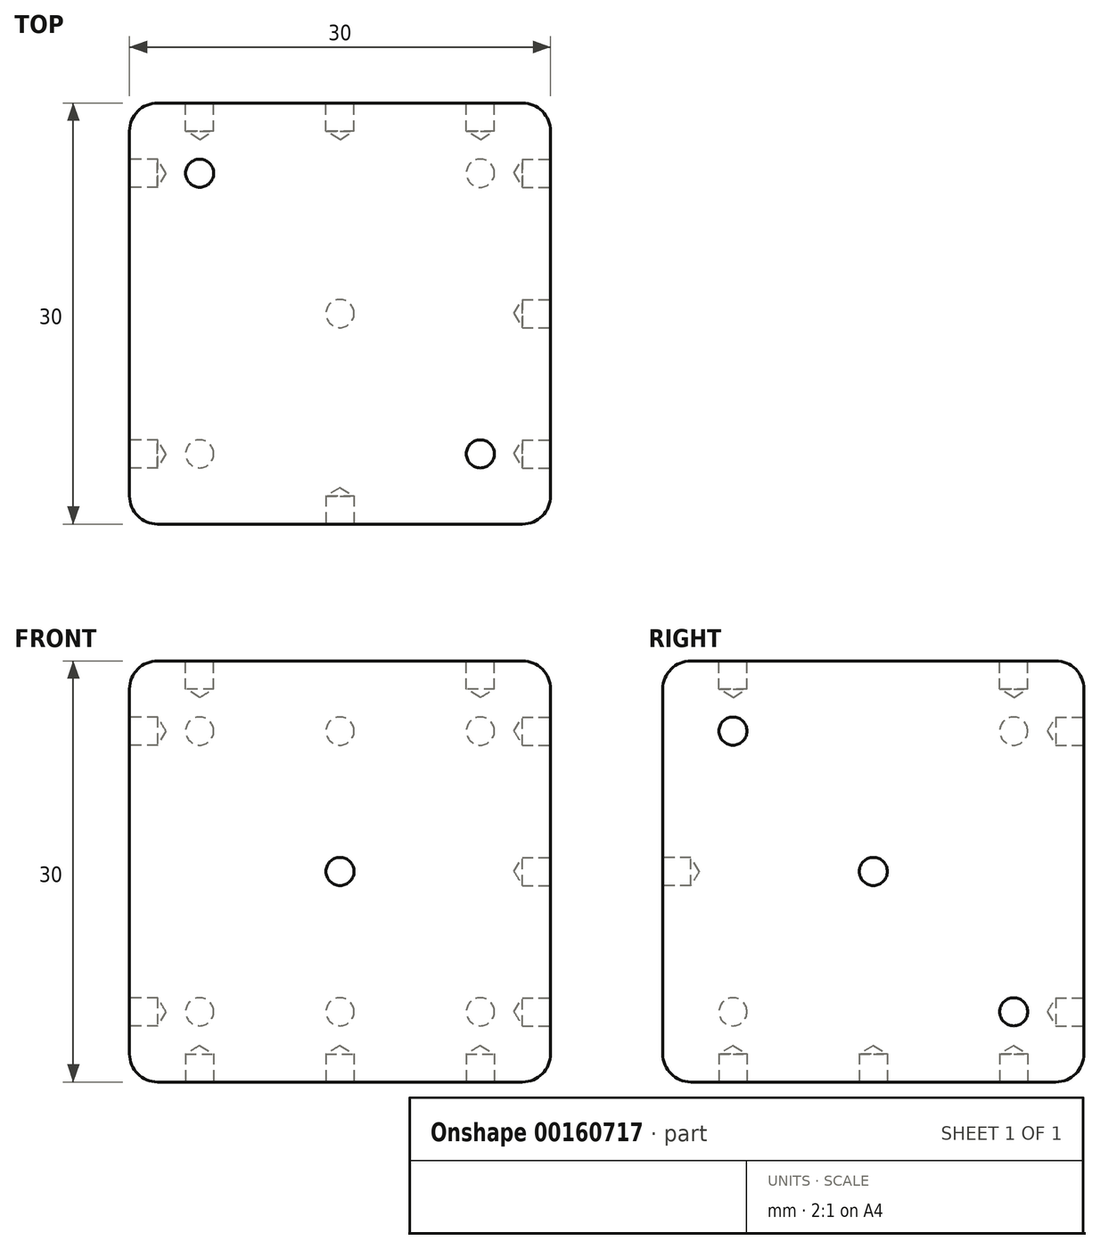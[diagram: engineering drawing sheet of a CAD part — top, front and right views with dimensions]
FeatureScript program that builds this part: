
annotation { "Feature Type Name" : "Feature", "Feature Type Description" : "" }
export const myFeature = defineFeature(function(context is Context, id is Id, definition is map)
    precondition{}
    {
        {
            var Q0;
            Q0=qCreatedBy(makeId("Front.planeOp"),FACE);
            var sketch = newSketch(context, id + "F0", { "sketchPlane" : qUnion([Q0])});
            skLineSegment(sketch, "E0.bottom", {"start": v(15, 15) * mm, "end": v(-15, 15) * mm});
            skLineSegment(sketch, "E0.top", {"start": v(15, -15) * mm, "end": v(-15, -15) * mm});
            skLineSegment(sketch, "E0.left", {"start": v(15, 15) * mm, "end": v(15, -15) * mm});
            skLineSegment(sketch, "E0.right", {"start": v(-15, 15) * mm, "end": v(-15, -15) * mm});
            skPoint(sketch, "E0.middle", {"position": v(0, 0) * mm});
            skSolve(sketch);
        }
        {
            var Q0;
            Q0 = qSketchRegion(id + "F0", true);
            extrude(context, id + "F1", {"entities" : qUnion([Q0]), "endBound" : BoundingType.SYMMETRIC, "depth" : 30 * mm});
        }
        {
            var Q0;
            Q0=makeQuery(id+"F1.opExtrude","CAP_EDGE",EDGE,{"disambiguationData":[OSD([sQuery(id+"F0.wireOp",EDGE,"E0.bottom")])],"isStart":false});
            var Q1;
            Q1=makeQuery(id+"F1.opExtrude","SWEPT_EDGE",EDGE,{"disambiguationData":[OSD([sQuery(id+"F0.wireOp",EDGE,"E0.bottom"),sQuery(id+"F0.wireOp",EDGE,"E0.left")])]});
            var Q2;
            Q2=makeQuery(id+"F1.opExtrude","CAP_EDGE",EDGE,{"disambiguationData":[OSD([sQuery(id+"F0.wireOp",EDGE,"E0.bottom")])],"isStart":true});
            var Q3;
            Q3=makeQuery(id+"F1.opExtrude","SWEPT_EDGE",EDGE,{"disambiguationData":[OSD([sQuery(id+"F0.wireOp",EDGE,"E0.bottom"),sQuery(id+"F0.wireOp",EDGE,"E0.right")])]});
            var Q4;
            Q4=makeQuery(id+"F1.opExtrude","CAP_EDGE",EDGE,{"disambiguationData":[OSD([sQuery(id+"F0.wireOp",EDGE,"E0.left")])],"isStart":false});
            var Q5;
            Q5=makeQuery(id+"F1.opExtrude","CAP_EDGE",EDGE,{"disambiguationData":[OSD([sQuery(id+"F0.wireOp",EDGE,"E0.top")])],"isStart":false});
            var Q6;
            Q6=makeQuery(id+"F1.opExtrude","CAP_EDGE",EDGE,{"disambiguationData":[OSD([sQuery(id+"F0.wireOp",EDGE,"E0.right")])],"isStart":false});
            var Q7;
            Q7=makeQuery(id+"F1.opExtrude","SWEPT_EDGE",EDGE,{"disambiguationData":[OSD([sQuery(id+"F0.wireOp",EDGE,"E0.top"),sQuery(id+"F0.wireOp",EDGE,"E0.left")])]});
            var Q8;
            Q8=makeQuery(id+"F1.opExtrude","CAP_EDGE",EDGE,{"disambiguationData":[OSD([sQuery(id+"F0.wireOp",EDGE,"E0.left")])],"isStart":true});
            var Q9;
            Q9=makeQuery(id+"F1.opExtrude","SWEPT_EDGE",EDGE,{"disambiguationData":[OSD([sQuery(id+"F0.wireOp",EDGE,"E0.top"),sQuery(id+"F0.wireOp",EDGE,"E0.right")])]});
            var Q10;
            Q10=makeQuery(id+"F1.opExtrude","CAP_EDGE",EDGE,{"disambiguationData":[OSD([sQuery(id+"F0.wireOp",EDGE,"E0.top")])],"isStart":true});
            var Q11;
            Q11=makeQuery(id+"F1.opExtrude","CAP_EDGE",EDGE,{"disambiguationData":[OSD([sQuery(id+"F0.wireOp",EDGE,"E0.right")])],"isStart":true});
            fillet(context, id + "F2", {"entities" : qUnion([Q0, Q1, Q2, Q3, Q4, Q5, Q6, Q7, Q8, Q9, Q10, Q11]), "radius" : 2 * mm, "tangentPropagation" : true, "allowEdgeOverflow" : false});
        }
        {
            var Q0;
            Q0=makeQuery(id+"F1.opExtrude","CAP_FACE",FACE,{"disambiguationData":[OSD([sQuery(id+"F0.wireOp",EDGE,"E0.bottom"),sQuery(id+"F0.wireOp",EDGE,"E0.top"),sQuery(id+"F0.wireOp",EDGE,"E0.left"),sQuery(id+"F0.wireOp",EDGE,"E0.right")])],"isStart":false});
            var sketch = newSketch(context, id + "F3", { "sketchPlane" : qUnion([Q0])});
            skCircle(sketch, "E1", {"center": v(0, 0) * mm, "radius": 1 * mm});
            skSolve(sketch);
        }
        {
            var Q0;
            Q0=sQuery(id+"F3.wireOp",VERTEX,"E1.center");
            var Q1;
            Q1=makeQuery(id+"F1.opExtrude","SWEPT_BODY",BODY,{"disambiguationData":[OSD([sQuery(id+"F0.wireOp",EDGE,"E0.bottom"),sQuery(id+"F0.wireOp",EDGE,"E0.top"),sQuery(id+"F0.wireOp",EDGE,"E0.left"),sQuery(id+"F0.wireOp",EDGE,"E0.right")])]});
            hole(context, id + "F4", {"style" : HoleStyle.SIMPLE, "endStyle" : HoleEndStyle.BLIND, "holeDiameter" : 2 * mm, "holeDepth" : 2 * mm, "locations" : qUnion([Q0]), "scope" : qUnion([Q1])});
        }
        {
            var Q0;
            Q0=makeQuery(id+"F1.opExtrude","SWEPT_FACE",FACE,{"disambiguationData":[OSD([sQuery(id+"F0.wireOp",EDGE,"E0.left")])]});
            var sketch = newSketch(context, id + "F5", { "sketchPlane" : qUnion([Q0])});
            skPoint(sketch, "E2", {"position": v(-10, 10) * mm});
            skPoint(sketch, "E3", {"position": v(10, -10) * mm});
            skPoint(sketch, "E4", {"position": v(0, 0) * mm});
            skSolve(sketch);
        }
        {
            var Q0;
            Q0=makeQuery(id+"F1.opExtrude","SWEPT_FACE",FACE,{"disambiguationData":[OSD([sQuery(id+"F0.wireOp",EDGE,"E0.bottom")])]});
            var sketch = newSketch(context, id + "F6", { "sketchPlane" : qUnion([Q0])});
            skPoint(sketch, "E5", {"position": v(-10, 10) * mm});
            skPoint(sketch, "E6", {"position": v(10, -10) * mm});
            skSolve(sketch);
        }
        {
            var Q0;
            Q0=makeQuery(id+"F1.opExtrude","SWEPT_FACE",FACE,{"disambiguationData":[OSD([sQuery(id+"F0.wireOp",EDGE,"E0.right")])]});
            var sketch = newSketch(context, id + "F7", { "sketchPlane" : qUnion([Q0])});
            skPoint(sketch, "E7", {"position": v(-10, 10) * mm});
            skPoint(sketch, "E8", {"position": v(10, 10) * mm});
            skPoint(sketch, "E9", {"position": v(10, -10) * mm});
            skPoint(sketch, "E10", {"position": v(-10, -10) * mm});
            skSolve(sketch);
        }
        {
            var Q0;
            Q0=makeQuery(id+"F1.opExtrude","CAP_FACE",FACE,{"disambiguationData":[OSD([sQuery(id+"F0.wireOp",EDGE,"E0.bottom"),sQuery(id+"F0.wireOp",EDGE,"E0.top"),sQuery(id+"F0.wireOp",EDGE,"E0.left"),sQuery(id+"F0.wireOp",EDGE,"E0.right")])],"isStart":true});
            var sketch = newSketch(context, id + "F8", { "sketchPlane" : qUnion([Q0])});
            skPoint(sketch, "E11", {"position": v(-10, -10) * mm});
            skPoint(sketch, "E12", {"position": v(10, -10) * mm});
            skPoint(sketch, "E13", {"position": v(10, 10) * mm});
            skPoint(sketch, "E14", {"position": v(0, 10) * mm});
            skPoint(sketch, "E15", {"position": v(-10, 10) * mm});
            skPoint(sketch, "E16", {"position": v(0, -10) * mm});
            skSolve(sketch);
        }
        {
            var Q0;
            Q0=makeQuery(id+"F1.opExtrude","SWEPT_FACE",FACE,{"disambiguationData":[OSD([sQuery(id+"F0.wireOp",EDGE,"E0.top")])]});
            var sketch = newSketch(context, id + "F9", { "sketchPlane" : qUnion([Q0])});
            skPoint(sketch, "E17", {"position": v(0, 0) * mm});
            skPoint(sketch, "E18", {"position": v(-10, 10) * mm});
            skPoint(sketch, "E19", {"position": v(10, 10) * mm});
            skPoint(sketch, "E20", {"position": v(10, -10) * mm});
            skPoint(sketch, "E21", {"position": v(-10, -10) * mm});
            skSolve(sketch);
        }
        {
            var Q0;
            Q0=sQuery(id+"F5.wireOp",VERTEX,"E2");
            var Q1;
            Q1=sQuery(id+"F5.wireOp",VERTEX,"E3");
            var Q2;
            Q2=sQuery(id+"F5.wireOp",VERTEX,"E4");
            var Q3;
            Q3=makeQuery(id+"F1.opExtrude","SWEPT_BODY",BODY,{"disambiguationData":[OSD([sQuery(id+"F0.wireOp",EDGE,"E0.bottom"),sQuery(id+"F0.wireOp",EDGE,"E0.top"),sQuery(id+"F0.wireOp",EDGE,"E0.left"),sQuery(id+"F0.wireOp",EDGE,"E0.right")])]});
            hole(context, id + "F10", {"style" : HoleStyle.SIMPLE, "endStyle" : HoleEndStyle.BLIND, "holeDiameter" : 2 * mm, "holeDepth" : 2 * mm, "startFromSketch" : true, "locations" : qUnion([Q0, Q1, Q2]), "scope" : qUnion([Q3])});
        }
        {
            var Q0;
            Q0=sQuery(id+"F8.wireOp",VERTEX,"E15");
            var Q1;
            Q1=sQuery(id+"F8.wireOp",VERTEX,"E14");
            var Q2;
            Q2=sQuery(id+"F8.wireOp",VERTEX,"E13");
            var Q3;
            Q3=sQuery(id+"F8.wireOp",VERTEX,"E12");
            var Q4;
            Q4=sQuery(id+"F8.wireOp",VERTEX,"E16");
            var Q5;
            Q5=sQuery(id+"F8.wireOp",VERTEX,"E11");
            var Q6;
            Q6=makeQuery(id+"F1.opExtrude","SWEPT_BODY",BODY,{"disambiguationData":[OSD([sQuery(id+"F0.wireOp",EDGE,"E0.bottom"),sQuery(id+"F0.wireOp",EDGE,"E0.top"),sQuery(id+"F0.wireOp",EDGE,"E0.left"),sQuery(id+"F0.wireOp",EDGE,"E0.right")])]});
            hole(context, id + "F11", {"style" : HoleStyle.SIMPLE, "endStyle" : HoleEndStyle.BLIND, "holeDiameter" : 2 * mm, "holeDepth" : 2 * mm, "startFromSketch" : true, "locations" : qUnion([Q0, Q1, Q2, Q3, Q4, Q5]), "scope" : qUnion([Q6])});
        }
        {
            var Q0;
            Q0=sQuery(id+"F6.wireOp",VERTEX,"E6");
            var Q1;
            Q1=sQuery(id+"F6.wireOp",VERTEX,"E5");
            var Q2;
            Q2=makeQuery(id+"F1.opExtrude","SWEPT_BODY",BODY,{"disambiguationData":[OSD([sQuery(id+"F0.wireOp",EDGE,"E0.bottom"),sQuery(id+"F0.wireOp",EDGE,"E0.top"),sQuery(id+"F0.wireOp",EDGE,"E0.left"),sQuery(id+"F0.wireOp",EDGE,"E0.right")])]});
            hole(context, id + "F12", {"style" : HoleStyle.SIMPLE, "endStyle" : HoleEndStyle.BLIND, "holeDiameter" : 2 * mm, "holeDepth" : 2 * mm, "startFromSketch" : true, "locations" : qUnion([Q0, Q1]), "scope" : qUnion([Q2])});
        }
        {
            var Q0;
            Q0=sQuery(id+"F7.wireOp",VERTEX,"E8");
            var Q1;
            Q1=sQuery(id+"F7.wireOp",VERTEX,"E7");
            var Q2;
            Q2=sQuery(id+"F7.wireOp",VERTEX,"E9");
            var Q3;
            Q3=sQuery(id+"F7.wireOp",VERTEX,"E10");
            var Q4;
            Q4=makeQuery(id+"F1.opExtrude","SWEPT_BODY",BODY,{"disambiguationData":[OSD([sQuery(id+"F0.wireOp",EDGE,"E0.bottom"),sQuery(id+"F0.wireOp",EDGE,"E0.top"),sQuery(id+"F0.wireOp",EDGE,"E0.left"),sQuery(id+"F0.wireOp",EDGE,"E0.right")])]});
            hole(context, id + "F13", {"style" : HoleStyle.SIMPLE, "endStyle" : HoleEndStyle.BLIND, "holeDiameter" : 2 * mm, "holeDepth" : 2 * mm, "startFromSketch" : true, "locations" : qUnion([Q0, Q1, Q2, Q3]), "scope" : qUnion([Q4])});
        }
        {
            var Q0;
            Q0=sQuery(id+"F9.wireOp",VERTEX,"E18");
            var Q1;
            Q1=sQuery(id+"F9.wireOp",VERTEX,"E21");
            var Q2;
            Q2=sQuery(id+"F9.wireOp",VERTEX,"E17");
            var Q3;
            Q3=sQuery(id+"F9.wireOp",VERTEX,"E20");
            var Q4;
            Q4=sQuery(id+"F9.wireOp",VERTEX,"E19");
            var Q5;
            Q5=makeQuery(id+"F1.opExtrude","SWEPT_BODY",BODY,{"disambiguationData":[OSD([sQuery(id+"F0.wireOp",EDGE,"E0.bottom"),sQuery(id+"F0.wireOp",EDGE,"E0.top"),sQuery(id+"F0.wireOp",EDGE,"E0.left"),sQuery(id+"F0.wireOp",EDGE,"E0.right")])]});
            hole(context, id + "F14", {"style" : HoleStyle.SIMPLE, "endStyle" : HoleEndStyle.BLIND, "holeDiameter" : 2 * mm, "holeDepth" : 2 * mm, "startFromSketch" : true, "locations" : qUnion([Q0, Q1, Q2, Q3, Q4]), "scope" : qUnion([Q5])});
        }
    });
